# Revit family: Podajnik_recznikow_ZZ DUO
name_source: partatom
category: Furniture
units: mm (PartAtom-declared; Revit-internal decimal feet)

## family parameters
Always vertical = Yes
Cut with Voids When Loaded = No
Host = Wall
Room Calculation Point = No
Shared = No

## types (1)
- Type 1
    Depth / Glebokosc = 120 mm  [stored 0.393701 ft]
    Description = Podajnik ręczników ZZ DUO to naścienny dozownik, wykonany ze stali nierdzewnej polerowanej. Jest niezwykle solidnym modelem o dużej pojemności, dzięki czemu świetnie zastępuje suszarki do rąk w toaletach publicznych z dużym natężeniem ruchu. Polerowana obudowa dodaje podajnikowi DUO elegancji, a wizjer w kształcie litery „S”, znajdujący się na jej środku, funkcjonalności. Dzięki niemu sprawdzanie poziomu ręczników w podajniku jest proste i niekłopotliwe. Wygodne jest również konserwowanie i czyszczenie pojemnika. Dozownik ręczników DUO to bardzo funkcjonalne urządzenie, które z powodzeniem zaspokoi potrzeby użytkowników.
    Height / Wysokosc = 270 mm  [stored 0.885827 ft]
    Manufacturer = FANECO.com
    Manufacturer code / Kod producenta = 5901764292555
    Material = Stal nierdzewna polerowana
    Material finish / Wykonczenie = Materiał Stal nierdzewna 430 polerowana
    Model = DUO
    Product code / Kod produktu = P600SJP
    URL = https://faneco.com
    Weight / Waga = 1.8 kg
    Width / Szerokosc = 270 mm  [stored 0.885827 ft]

note: [stored X ft] marks values corroborated as IEEE doubles in the binary element streams (Revit-internal decimal feet)

## geometry (parser evidence)
native form markers: Blend x4, Sweep x6
no freeform markers — native parametric forms only
